# Revit family: WINMASTER_KONSOLBESLAG
name_source: partatom
category: Detail Items
units: mm (PartAtom-declared; Revit-internal decimal feet)

## family parameters
Rotate with component = No
Section Shape = Not Defined
Shared = Yes

## types (1)
- WINMASTER_KONSOLBESLAG
    Anvendelse = Beton, mursten og gasbeton
    Brandklasse af pladefalsen = Brandklasse A1
    Bredder af bærebeslag = 9mm, 12mm, 15mm, 18mm, 21mm, 24mm, 27mm
    Bæreevne af bærebeslag = optil 100 kg pr. beslag
    Description = Bundsamling m. bærebeslag (vindue)
    Funktion = Understøtter vinduet i forbindelse med montage
    Galvaniseret stål = Klasse 2-3
    Linjetab af pladefalse = 0,33 W/mK
    Længe af bærebeslag = Længde kan
Længe kan justeres (spring i længder er 30 mm)
    Manufacturer = WINMASTER
    Material_Bærebeslag = Rustfri Stål (tilkøb klasse 5)
    Material_Harpun Klods = Plast
    Material_Isolering = PU Skum
    Material_Mørtel = Limmørtel
    Material_Pladefalsen = Lysningsplade
    Samling as pladefelsen = Tappes ind i hinanden for at sikre
stabillitet og placering.

Tappes ind i hinanden for at sikre
stabillitet og placering. Hjørner skal beklædes med net. Samling i hjørner med LIP
HJØRNEARMERING
    Tykkelse af bærebeslag = 2 mm
    URL = https://winmaster.dk
    Udført af = Tegnestuen Tankestregen
    WINMASTER_Bærebeslag = https://winmaster.dk
    WINMASTER_Pladefalse = https://winmaster.dk
    WINMASTER_URL = https://winmaster.dk

## geometry (parser evidence)
native form markers: Sweep x25
no freeform markers — native parametric forms only
